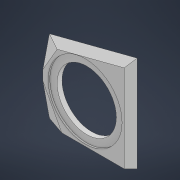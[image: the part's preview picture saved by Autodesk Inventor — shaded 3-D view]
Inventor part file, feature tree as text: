
AUTODESK INVENTOR PART (.ipt)
format: ipt  version: 2022 (Build 260153000, 153)  size: 138,752 bytes
history: native  units: mm
features: sketch x4, other x4, extrude x2, chamfer x1
ambient origin geometry x8: Origin, YZ Plane, XZ Plane, XY Plane, X Axis, Y Axis, Z Axis, Center Point
bodies: Body1 (feature_tree)
feature tree (11):
  sketch  "Эскиз1"
  extrude  "Выдавливание2"  Depth=12.0mm TaperAngle=0.0deg
  extrude  "Выдавливание3"  Depth=16.0mm TaperAngle=0.0deg
  sketch  "Эскиз4"
  sketch  "Эскиз5"
  other  "РабПлоскость1"
  other  "Разделение1"
  sketch  "Эскиз6"
  other  "РабПлоскость2"
  other  "Разделение2"
  chamfer  "Фаска1"  Distance=48.0mm
